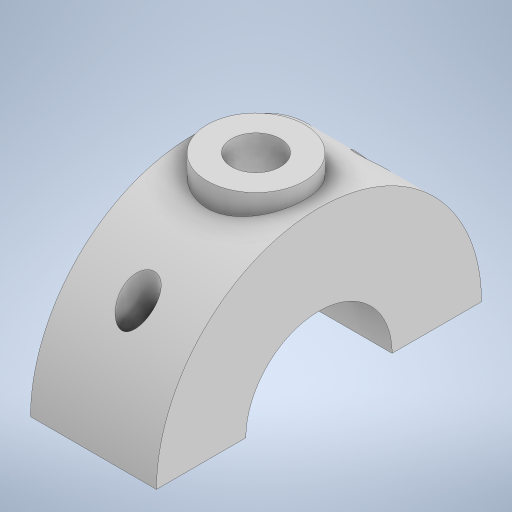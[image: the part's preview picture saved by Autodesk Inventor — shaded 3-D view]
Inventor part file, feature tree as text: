
AUTODESK INVENTOR PART (.ipt)
format: ipt  version: 2023 (Build 270158000, 158)  size: 296,448 bytes
history: native  units: mm
features: extrude x6, sketch x4, projected_geometry x4, plane x3
ambient origin geometry x8: Origin, YZ Plane, XZ Plane, XY Plane, X Axis, Y Axis, Z Axis, Center Point
bodies: Solid1 (feature_tree)
feature tree (17):
  extrude  "Extrusion1"  Depth=40.0mm
  plane  "Work Plane1"
  sketch  "Sketch2"  dims[d4=15.5mm d5=0.0mm d6=6.0mm]
  extrude  "Extrusion2"  Depth=6.0mm
  extrude  "Extrusion3"  Depth=15.5mm TaperAngle=0.0deg
  extrude  "Extrusion4"  TaperAngle=0.0deg  [1 undecoded]
  plane  "Work Plane2"
  extrude  "Extrusion5"  Depth=10.0mm
  plane  "Work Plane3"
  extrude  "Extrusion6"  Depth=10.0mm TaperAngle=0.0deg
  sketch  "Sketch1"  dims[d0=18.0mm d1=40.0mm]
  projected_geometry  "Projected Loop1"
  sketch  "Sketch3"  dims[d7=12.0mm d8=15.5mm d9=0.0mm]
  projected_geometry  "Projected Loop2"
  sketch  "Sketch4"  dims[d10=2.0mm d11=0.0mm d12=0.0mm d13=0.0mm d14=10.0mm d15=20.4mm d16=0.0mm d19=4.0mm d20=4.0mm d21=0.0mm d22=0.0mm d23=11.0mm d24=11.0mm]
  projected_geometry  "Projected Loop3"
  projected_geometry  "Projected Loop4"
note: 1 required parameter value undecoded (feature->parameter linkage not recoverable at this tier; creation-order binding heuristic only, values carry confidence <= 0.55)
